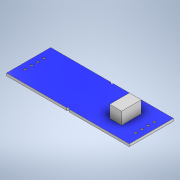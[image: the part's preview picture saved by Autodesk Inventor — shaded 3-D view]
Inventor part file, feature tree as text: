
AUTODESK INVENTOR PART (.ipt)
format: ipt  version: 2020 (Build 240168000, 168)  size: 148,992 bytes
history: native  units: mm
features: other x9, sketch x3, extrude x2, hole x1
ambient origin geometry x8: Origin, YZ Plane, XZ Plane, XY Plane, X Axis, Y Axis, Z Axis, Center Point
bodies: Body1 (feature_tree)
feature tree (15):
  other  "Sólido1"
  extrude  "Extrusión1"  Depth=18.0mm
  hole  "Agujero1"  [1 undecoded]
  extrude  "Extrusión2"  Depth=5.0mm
  other  "Eje de trabajo1"
  other  "Eje de trabajo2"
  other  "Eje de trabajo3"
  other  "Eje de trabajo4"
  other  "Eje de trabajo5"
  other  "Eje de trabajo6"
  other  "Eje de trabajo7"
  other  "Eje de trabajo8"
  sketch  "Boceto1"  dims[d0=1.0mm d1=18.0mm]
  sketch  "Boceto2"  dims[d2=9.0mm d3=0.5mm]
  sketch  "Boceto3"  dims[d4=50.0mm d5=0.0mm d6=5.19mm d8=2.54mm d9=2.54mm d10=2.54mm d11=2.54mm d12=0.9mm d13=6.0mm d14=4.0mm d15=2.0mm d16=90.0deg d17=8.0mm d18=20.594885mm d19=5.0mm d20=5.0mm d21=5.0mm d22=0.0mm d23=0.375mm]
note: 1 required parameter value undecoded (feature->parameter linkage not recoverable at this tier; creation-order binding heuristic only, values carry confidence <= 0.55)
